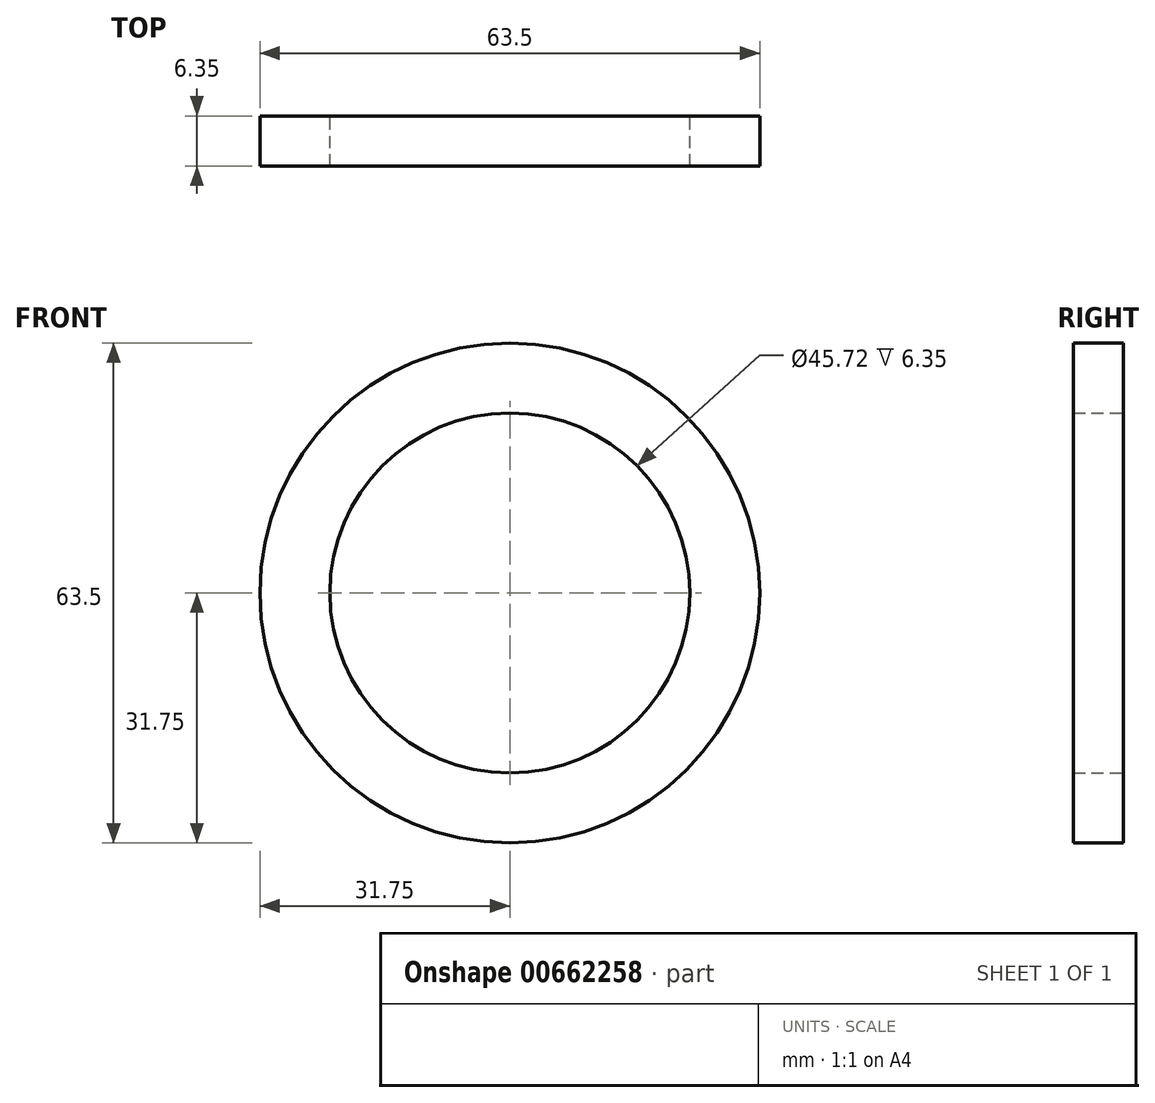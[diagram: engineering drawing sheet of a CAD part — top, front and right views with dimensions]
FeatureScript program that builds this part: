
annotation { "Feature Type Name" : "Feature", "Feature Type Description" : "" }
export const myFeature = defineFeature(function(context is Context, id is Id, definition is map)
    precondition{}
    {
        {
            var Q0;
            Q0=qCreatedBy(makeId("Front.planeOp"),FACE);
            var sketch = newSketch(context, id + "F0", { "sketchPlane" : qUnion([Q0])});
            skCircle(sketch, "E0", {"center": v(0, 0) * mm, "radius": 22.86 * mm});
            skCircle(sketch, "E1", {"center": v(0, 0) * mm, "radius": 31.75 * mm});
            skSolve(sketch);
        }
        {
            var Q0;
            Q0 = qSketchRegion(id + "F0", true);
            extrude(context, id + "F1", {"entities" : qUnion([Q0]), "depth" : 6.35 * mm, "offsetDistance" : 25.4 * mm});
        }
    });
